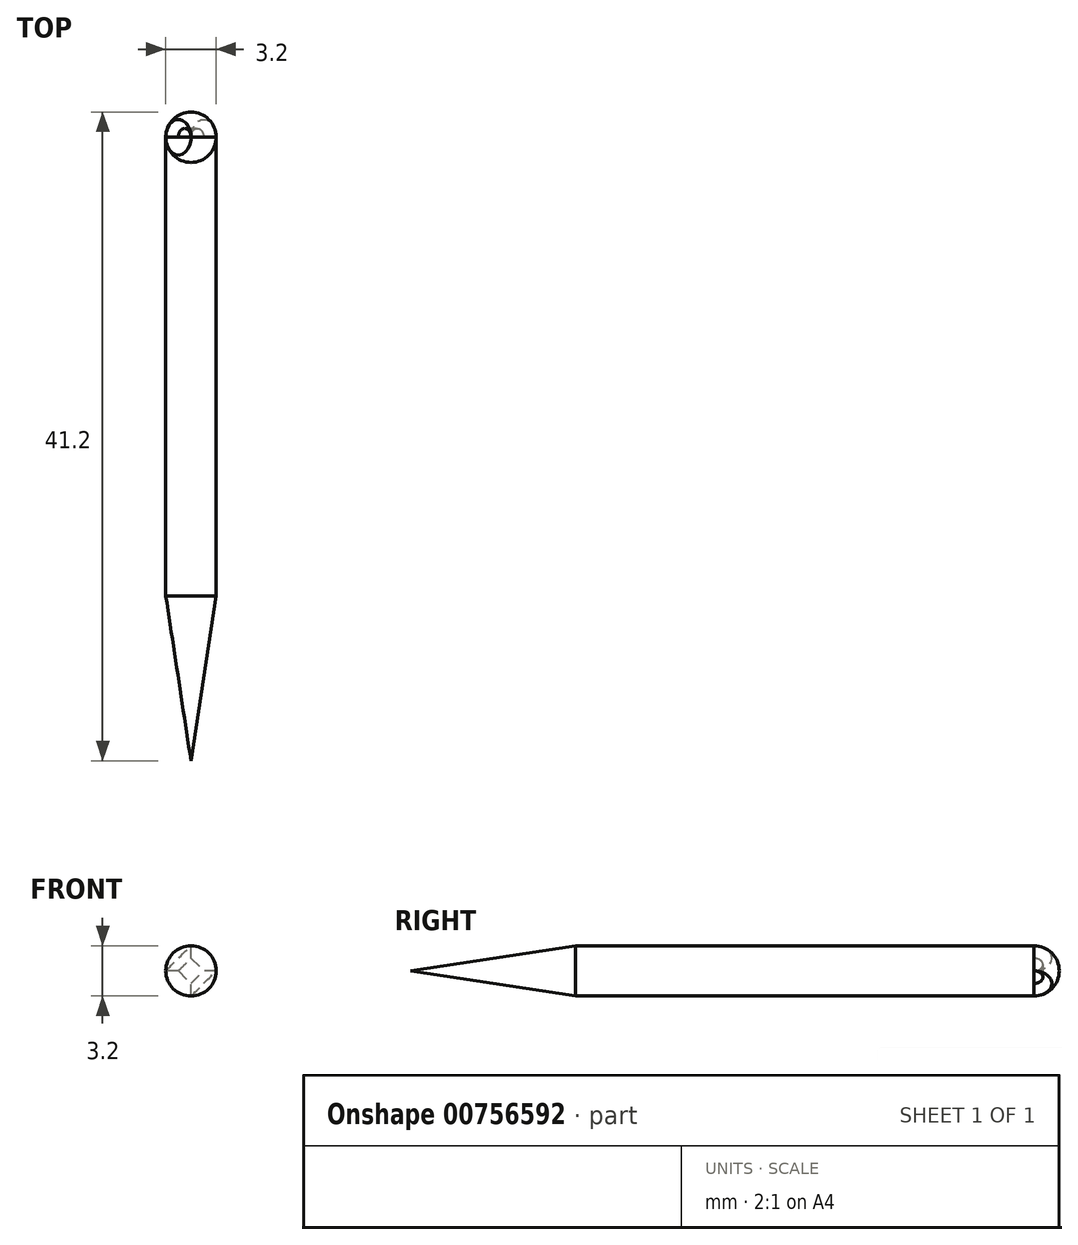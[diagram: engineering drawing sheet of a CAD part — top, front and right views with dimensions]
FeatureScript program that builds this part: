
annotation { "Feature Type Name" : "Feature", "Feature Type Description" : "" }
export const myFeature = defineFeature(function(context is Context, id is Id, definition is map)
    precondition{}
    {
        {
            var Q0;
            Q0=qCreatedBy(makeId("Top.planeOp"),FACE);
            var sketch = newSketch(context, id + "F0", { "sketchPlane" : qUnion([Q0])});
            skLineSegment(sketch, "E0.right", {"start": v(-4.34, 35.09) * mm, "end": v(-4.34, 5.96) * mm});
            skPoint(sketch, "E1.orphan", {"position": v(-4.34, 37.49) * mm});
            skPoint(sketch, "E2.orphan", {"position": v(-7.54, 37.49) * mm});
            skPoint(sketch, "E3.orphan", {"position": v(-7.54, -4.51) * mm});
            skPoint(sketch, "E4.orphan", {"position": v(-4.34, -4.51) * mm});
            skPoint(sketch, "E5.start.orphan", {"position": v(-7.54, 0.29) * mm});
            skLineSegment(sketch, "E6.trimOffspring", {"start": v(-5.94, 31.89) * mm, "end": v(-5.94, -4.51) * mm});
            skLineSegment(sketch, "E7", {"start": v(-4.34, 5.96) * mm, "end": v(-5.94, -4.51) * mm});
            skPoint(sketch, "E8.end.orphan", {"position": v(-4.34, 0.29) * mm});
            skLineSegment(sketch, "E9", {"start": v(-5.94, 35.09) * mm, "end": v(-5.94, 31.89) * mm});
            skLineSegment(sketch, "E10", {"start": v(-4.34, 35.09) * mm, "end": v(-5.94, 35.09) * mm});
            skLineSegment(sketch, "E11", {"start": v(-5.94, 35.09) * mm, "end": v(-5.14, 35.09) * mm});
            skLineSegment(sketch, "E12", {"start": v(-5.14, 35.09) * mm, "end": v(-5.94, 35.09) * mm});
            skPoint(sketch, "E13.1.internal.orphan", {"position": v(-5.94, 37.49) * mm});
            skPoint(sketch, "E14.orphan", {"position": v(-7.54, 35.09) * mm});
            skSolve(sketch);
        }
        {
            var Q0;
            {var subQ1=sQuery(id+"F0.wireOp",EDGE,"E0.right");Q0=makeQuery(id+"F0.imprint","IMPRINT",FACE,{"disambiguationData":[TD([[makeQuery(id+"F0.imprint","IMPRINT",EDGE,{"derivedFrom":subQ1}),-1.0]])]});}
            var Q1;
            Q1=sQuery(id+"F0.wireOp",EDGE,"E6.trimOffspring");
            revolve(context, id + "F1", {"surfaceOperationType" : NewSurfaceOperationType.NEW, "entities" : qUnion([Q0]), "axis" : qUnion([Q1]), "revolveType" : RevolveType.FULL});
        }
        {
            var Q0;
            Q0=makeQuery(id+"F1.opRevolve","SWEPT_FACE",FACE,{"disambiguationData":[OSD([sQuery(id+"F0.wireOp",EDGE,"E10"),sQuery(id+"F0.wireOp",EDGE,"E12")])]});
            var sketch = newSketch(context, id + "F2", { "sketchPlane" : qUnion([Q0])});
            skLineSegment(sketch, "E15", {"start": v(4.34, 0) * mm, "end": v(5.14, 0) * mm});
            skLineSegment(sketch, "E16", {"start": v(5.94, 0.8) * mm, "end": v(5.94, 1.6) * mm});
            skLineSegment(sketch, "E17", {"start": v(5.94, 0.8) * mm, "end": v(5.14, 0) * mm});
            skPoint(sketch, "E18.orphan", {"position": v(5.94, 0) * mm});
            skLineSegment(sketch, "E19", {"start": v(5.94, 0) * mm, "end": v(4.8, 1.13) * mm});
            skLineSegment(sketch, "E20", {"start": v(5.94, 0) * mm, "end": v(7.07, 1.13) * mm});
            skLineSegment(sketch, "E21", {"start": v(7.07, 1.13) * mm, "end": v(4.8, -1.13) * mm});
            skSolve(sketch);
        }
        {
            var Q0;
            {var subQ0=sQuery(id+"F2.wireOp",EDGE,"E16");Q0=makeQuery(id+"F2.imprint","IMPRINT",FACE,{"disambiguationData":[TD([[makeQuery(id+"F2.imprint","IMPRINT",EDGE,{"derivedFrom":subQ0}),1.0]])]});}
            var Q1;
            {var subQ0=sQuery(id+"F2.wireOp",EDGE,"E15");Q1=makeQuery(id+"F2.imprint","IMPRINT",FACE,{"disambiguationData":[TD([[makeQuery(id+"F2.imprint","IMPRINT",EDGE,{"derivedFrom":subQ0}),1.0]])]});}
            var Q2;
            Q2=sQuery(id+"F2.wireOp",EDGE,"E21");
            revolve(context, id + "F3", {"surfaceOperationType" : NewSurfaceOperationType.NEW, "entities" : qUnion([Q0, Q1]), "axis" : qUnion([Q2]), "revolveType" : RevolveType.ONE_DIRECTION, "oppositeDirection" : true, "angle" : 180 * degree});
        }
    });
